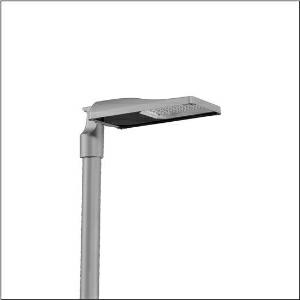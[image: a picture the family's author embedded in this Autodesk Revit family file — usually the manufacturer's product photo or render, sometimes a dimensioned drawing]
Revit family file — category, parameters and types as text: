
# Revit family: streetlight_sl_31_mini___st1_0a_5xh2d71b08ja_2c97
name_source: partatom
category: Lighting Fixtures
units: mm (PartAtom-declared; Revit-internal decimal feet)

## family parameters
Cut with Voids When Loaded = No
Host = Face
Light Source = No
Part Type = Normal
Room Calculation Point = No
Round Connector Dimension = Use Diameter
Shared = No

## types (1)
- --- (1 x LED, 9800 lm, 81.1 W, 2200K)
    Apparent Load = 81 VA
    CIE Flux Codes = 40 73 97 100 100
    Color Rendering = 70
    Color Temperature = 2200K
    Default Elevation = 1800 mm
    Description = Streetlight SL 31 mini Easy, LST, Desk-Remote mast luminaire for post-top, side-entry; light control with lens of PMMA; light distribution: ST1.0a, direct asymmetric distribution, for standard-compliant lighting for roads and squares; LED: luminous flux: 9.800lm, light colour: 722, colour temperature: 2200K; luminous efficacy: 120,8lm/W; control: pre-setting: linear dimming characteristic, flexible luminous flux parameterisation, time-dependent luminous flux control, constant luminous flux control, power reduction, intelligent temperature release in ECG and LED module, overheat protection; luminaire housing, of diecast aluminium, Siteco® metallic grey (DB 702S), corrosivity category C5 high according to DIN EN ISO 12944; cover of toughened safety glass, transparent, mast flange of diecast aluminium, Siteco® metallic grey (DB 702S), spigot size: 76/60mm, mast flange included unmounted; with cable H07RN-F 3x 1.5mm², cable length: 10,5m, connection cable pre-assembled; mains connection: 220..240V, AC, 50/60Hz; power consumption (at start of service life): 81,1W / (at end of service life): 88,3W / (with reduced operation 50%): 36,1W; protection rating (complete): IP66; insulation class (complete): insulation class II (safety insulation); impact resistance: IK10; certification: CE, ENEC, ENEC+, VDE, UKCA; permissible operating ambient temperature for outdoor applications: -40..+50°C; packaging unit: 1 piece

Light Distribution: ST1.0a
    Height = 76 mm
    Lamp = 1 x LED
    Lamp Light Flux = 9800 lm
    Lamp Power = 81.1 W
    Lamp count = 1
    Length = 547 mm
    Luminous efficacy = 121 lm/W
    Manufacturer = Siteco
    ModVariant = No
    Model = 5XH2D71B08JA
    Number of Poles = 1
    OnlyDefault = Yes
    Power Factor = 1
    Product Name = Streetlight SL 31 mini | ST1.0a
    Product group = mast luminaire | pylon top
    ProductGroupID = 6100
    Protection Class = Protection class II
    Protection Degree = IP 66
    RLX_Detail_Level = 1
    RLX_Emergency_Light_Flux = 0 lm
    RLX_Emergency_Type = 0
    RLX_Emergency_Type_DB = No
    RlxData = <blob elided: 39545 chars, md5=eb7459b4>
    Socket = socket
    Standby Power = 0 W
    System Light Flux = 9800 lm
    System Power = 81 W
    Type Comments = factory setting: luminous flux: 100 % | dim-lin: 254 | 860 mA
    Type Image = l_1300326.jpg
    URL = http://relux.com
    VarID = @adj_008589
    Voltage = 0 V
    Weight = 0.00 kg
    Width = 265 mm

## geometry (parser evidence)
native form markers: Blend x4, Sweep x9
no freeform markers — native parametric forms only
